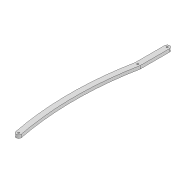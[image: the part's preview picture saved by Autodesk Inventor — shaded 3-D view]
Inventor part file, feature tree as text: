
AUTODESK INVENTOR PART (.ipt)
format: ipt  version: 2022 (Build 260153000, 153)  size: 99,840 bytes
history: native  units: mm
features: extrude x1, sketch x1
ambient origin geometry x8: Origin, YZ Plane, XZ Plane, XY Plane, X Axis, Y Axis, Z Axis, Center Point
bodies: Solid1 (feature_tree)
feature tree (2):
  extrude  "Extrusion1"  Depth=600.0mm
  sketch  "Sketch1"  dims[d0=3.3mm d1=3.3mm d2=10.0mm d3=288.984mm d6=6.0mm d7=0.0mm d14=3.3mm d15=231.585mm d18=600.0mm d19=600.0mm]
